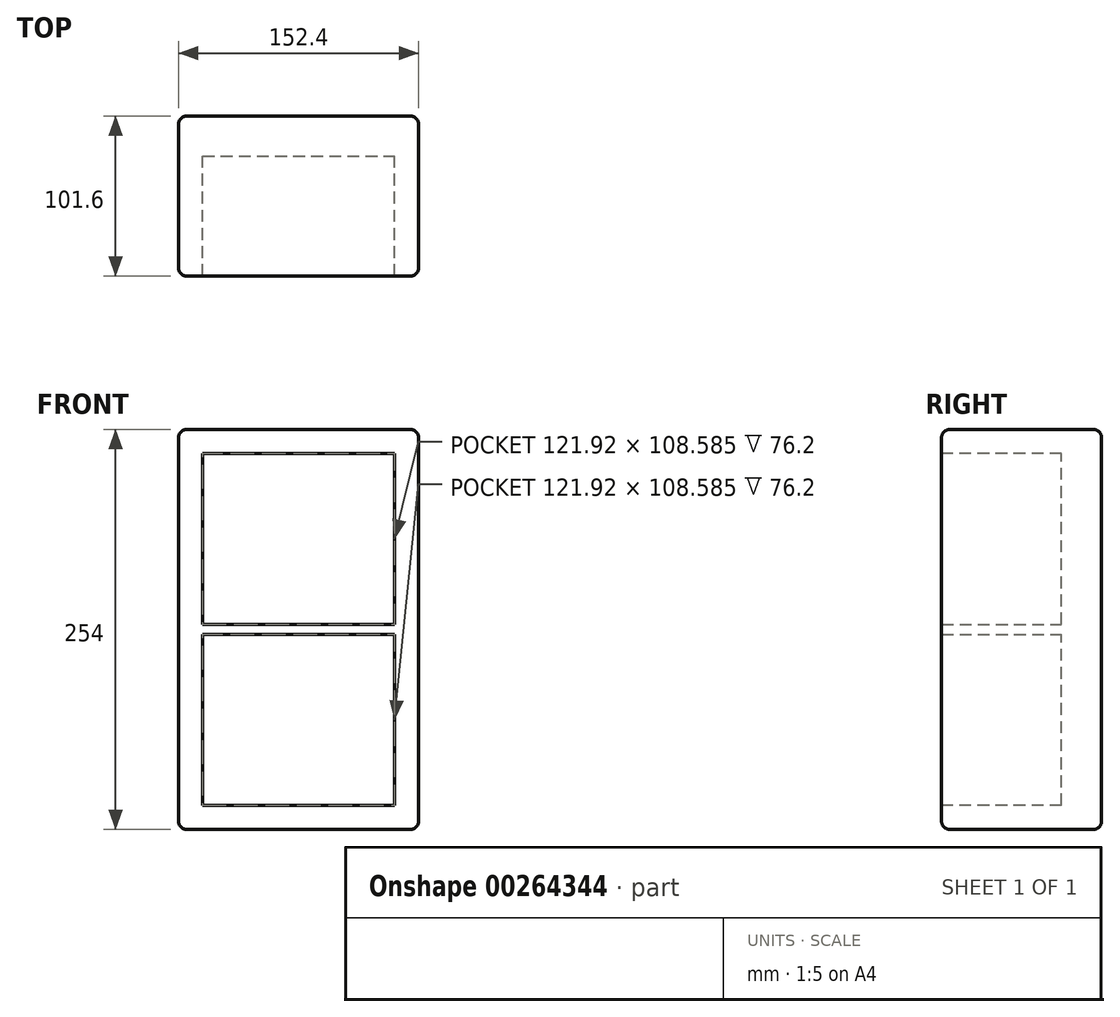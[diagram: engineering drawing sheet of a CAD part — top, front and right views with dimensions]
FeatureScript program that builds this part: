
annotation { "Feature Type Name" : "Feature", "Feature Type Description" : "" }
export const myFeature = defineFeature(function(context is Context, id is Id, definition is map)
    precondition{}
    {
        {
            var Q0;
            Q0=qCreatedBy(makeId("Top.planeOp"),FACE);
            var sketch = newSketch(context, id + "F0", { "sketchPlane" : qUnion([Q0])});
            skLineSegment(sketch, "E0.bottom", {"start": v(-76.2, -50.8) * mm, "end": v(76.2, -50.8) * mm});
            skLineSegment(sketch, "E0.top", {"start": v(-76.2, 50.8) * mm, "end": v(76.2, 50.8) * mm});
            skLineSegment(sketch, "E0.left", {"start": v(-76.2, -50.8) * mm, "end": v(-76.2, 50.8) * mm});
            skLineSegment(sketch, "E0.right", {"start": v(76.2, -50.8) * mm, "end": v(76.2, 50.8) * mm});
            skPoint(sketch, "E0.middle", {"position": v(0, 0) * mm});
            skLineSegment(sketch, "E1.top", {"start": v(-68.3, 40.23) * mm, "end": v(68.3, 40.23) * mm});
            skLineSegment(sketch, "E1.left", {"start": v(-68.3, -40.23) * mm, "end": v(-68.3, 40.23) * mm});
            skLineSegment(sketch, "E1.right", {"start": v(68.3, -40.23) * mm, "end": v(68.3, 40.23) * mm});
            skLineSegment(sketch, "E2.bottom", {"start": v(-68.3, -50.8) * mm, "end": v(68.3, -50.8) * mm});
            skLineSegment(sketch, "E2.left", {"start": v(-68.3, -50.8) * mm, "end": v(-68.3, -40.48) * mm});
            skLineSegment(sketch, "E2.right", {"start": v(68.3, -50.8) * mm, "end": v(68.3, -40.48) * mm});
            skSolve(sketch);
        }
        {
            var Q0;
            Q0=makeQuery(id+"F0.imprint","IMPRINT",FACE,{"disambiguationData":[TD([[makeQuery(id+"F0.imprint","IMPRINT",EDGE,{"derivedFrom":sQuery(id+"F0.wireOp",EDGE,"E0.bottom")}),1.0]])]});
            extrude(context, id + "F1", {"entities" : qUnion([Q0]), "endBound" : BoundingType.SYMMETRIC, "depth" : 254 * mm});
        }
        {
            var Q0;
            Q0=makeQuery(id+"F1.opExtrude","SWEPT_FACE",FACE,{"disambiguationData":[OSD([sQuery(id+"F0.wireOp",EDGE,"E0.bottom"),sQuery(id+"F0.wireOp",EDGE,"E2.bottom")])]});
            var sketch = newSketch(context, id + "F2", { "sketchPlane" : qUnion([Q0])});
            skLineSegment(sketch, "E3.bottom", {"start": v(-60.96, -111.76) * mm, "end": v(60.96, -111.76) * mm});
            skLineSegment(sketch, "E3.top", {"start": v(-60.96, 111.76) * mm, "end": v(60.96, 111.76) * mm});
            skLineSegment(sketch, "E3.left", {"start": v(-60.96, -111.76) * mm, "end": v(-60.96, 111.76) * mm});
            skLineSegment(sketch, "E3.right", {"start": v(60.96, -111.76) * mm, "end": v(60.96, 111.76) * mm});
            skPoint(sketch, "E3.middle", {"position": v(0, 0) * mm});
            skSolve(sketch);
        }
        {
            var Q0;
            Q0=makeQuery(id+"F2.imprint","IMPRINT",FACE,{"disambiguationData":[TD([[makeQuery(id+"F2.imprint","IMPRINT",EDGE,{"derivedFrom":sQuery(id+"F2.wireOp",EDGE,"E3.bottom")}),1.0]])]});
            extrude(context, id + "F3", {"entities" : qUnion([Q0]), "operationType" : NewBodyOperationType.REMOVE, "oppositeDirection" : true, "depth" : 76.2 * mm});
        }
        {
            var Q0;
            Q0=makeQuery(id+"F1.opExtrude","CAP_EDGE",EDGE,{"disambiguationData":[OSD([sQuery(id+"F0.wireOp",EDGE,"E0.right")])],"isStart":false});
            var Q1;
            Q1=makeQuery(id+"F1.opExtrude","CAP_EDGE",EDGE,{"disambiguationData":[OSD([sQuery(id+"F0.wireOp",EDGE,"E0.bottom"),sQuery(id+"F0.wireOp",EDGE,"E2.bottom")])],"isStart":false});
            var Q2;
            Q2=makeQuery(id+"F1.opExtrude","CAP_EDGE",EDGE,{"disambiguationData":[OSD([sQuery(id+"F0.wireOp",EDGE,"E0.left")])],"isStart":false});
            var Q3;
            Q3=makeQuery(id+"F1.opExtrude","CAP_EDGE",EDGE,{"disambiguationData":[OSD([sQuery(id+"F0.wireOp",EDGE,"E0.top")])],"isStart":false});
            var Q4;
            Q4=makeQuery(id+"F1.opExtrude","SWEPT_EDGE",EDGE,{"disambiguationData":[OSD([sQuery(id+"F0.wireOp",EDGE,"E0.bottom"),sQuery(id+"F0.wireOp",EDGE,"E0.right")])]});
            var Q5;
            Q5=makeQuery(id+"F1.opExtrude","SWEPT_EDGE",EDGE,{"disambiguationData":[OSD([sQuery(id+"F0.wireOp",EDGE,"E0.bottom"),sQuery(id+"F0.wireOp",EDGE,"E0.left")])]});
            var Q6;
            Q6=makeQuery(id+"F1.opExtrude","SWEPT_EDGE",EDGE,{"disambiguationData":[OSD([sQuery(id+"F0.wireOp",EDGE,"E0.top"),sQuery(id+"F0.wireOp",EDGE,"E0.right")])]});
            var Q7;
            Q7=makeQuery(id+"F1.opExtrude","CAP_EDGE",EDGE,{"disambiguationData":[OSD([sQuery(id+"F0.wireOp",EDGE,"E0.right")])],"isStart":true});
            var Q8;
            Q8=makeQuery(id+"F1.opExtrude","CAP_EDGE",EDGE,{"disambiguationData":[OSD([sQuery(id+"F0.wireOp",EDGE,"E0.bottom"),sQuery(id+"F0.wireOp",EDGE,"E2.bottom")])],"isStart":true});
            var Q9;
            Q9=makeQuery(id+"F1.opExtrude","SWEPT_EDGE",EDGE,{"disambiguationData":[OSD([sQuery(id+"F0.wireOp",EDGE,"E0.top"),sQuery(id+"F0.wireOp",EDGE,"E0.left")])]});
            var Q10;
            Q10=makeQuery(id+"F1.opExtrude","CAP_EDGE",EDGE,{"disambiguationData":[OSD([sQuery(id+"F0.wireOp",EDGE,"E0.top")])],"isStart":true});
            var Q11;
            Q11=makeQuery(id+"F1.opExtrude","CAP_EDGE",EDGE,{"disambiguationData":[OSD([sQuery(id+"F0.wireOp",EDGE,"E0.left")])],"isStart":true});
            fillet(context, id + "F4", {"entities" : qUnion([Q0, Q1, Q2, Q3, Q4, Q5, Q6, Q7, Q8, Q9, Q10, Q11]), "radius" : 5.08 * mm, "tangentPropagation" : true, "allowEdgeOverflow" : false});
        }
        {
            var Q0;
            Q0=makeQuery(id+"F3.boolean.opBoolean","COPY",FACE,{"derivedFrom":makeQuery(id+"F3.opExtrude","CAP_FACE",FACE,{"disambiguationData":[OSD([sQuery(id+"F2.wireOp",EDGE,"E3.bottom"),sQuery(id+"F2.wireOp",EDGE,"E3.top"),sQuery(id+"F2.wireOp",EDGE,"E3.left"),sQuery(id+"F2.wireOp",EDGE,"E3.right")])],"isStart":false})});
            var sketch = newSketch(context, id + "F5", { "sketchPlane" : qUnion([Q0])});
            skLineSegment(sketch, "E4.bottom", {"start": v(-60.96, -3.18) * mm, "end": v(60.96, -3.18) * mm});
            skLineSegment(sketch, "E4.top", {"start": v(-60.96, 3.17) * mm, "end": v(60.96, 3.17) * mm});
            skLineSegment(sketch, "E4.left", {"start": v(-60.96, -3.18) * mm, "end": v(-60.96, 3.17) * mm});
            skLineSegment(sketch, "E4.right", {"start": v(60.96, -3.18) * mm, "end": v(60.96, 3.17) * mm});
            skPoint(sketch, "E4.middle", {"position": v(0, 0) * mm});
            skSolve(sketch);
        }
        {
            var Q0;
            Q0=makeQuery(id+"F5.imprint","IMPRINT",FACE,{"disambiguationData":[TD([[makeQuery(id+"F5.imprint","IMPRINT",EDGE,{"derivedFrom":sQuery(id+"F5.wireOp",EDGE,"E4.bottom")}),1.0]])]});
            extrude(context, id + "F6", {"entities" : qUnion([Q0]), "operationType" : NewBodyOperationType.ADD, "depth" : 76.2 * mm});
        }
    });
